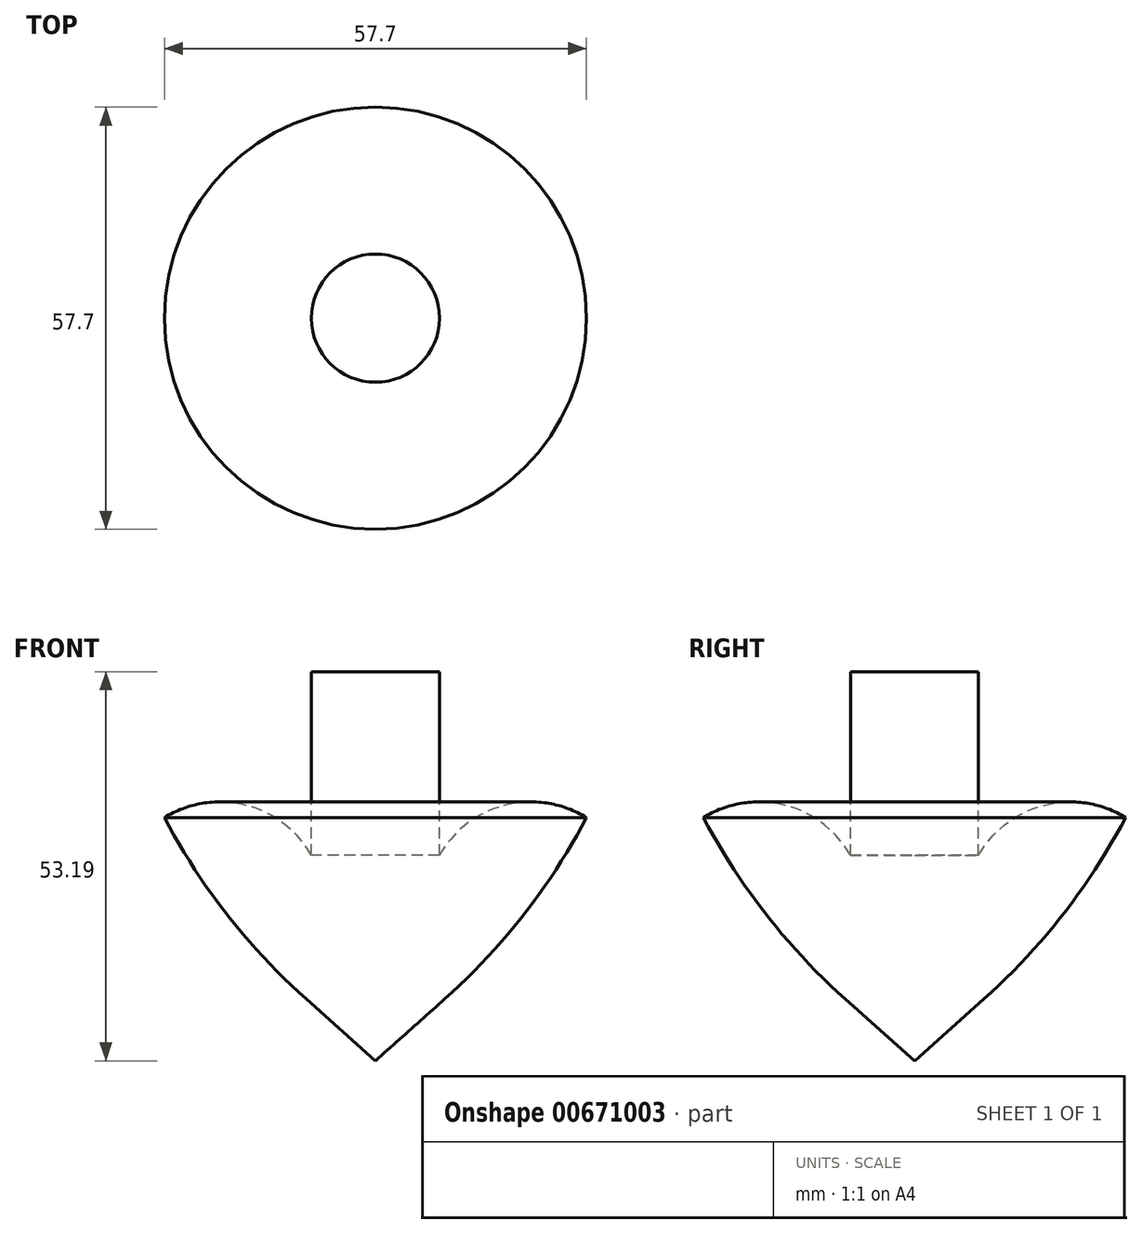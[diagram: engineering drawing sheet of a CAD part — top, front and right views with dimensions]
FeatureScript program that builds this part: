
annotation { "Feature Type Name" : "Feature", "Feature Type Description" : "" }
export const myFeature = defineFeature(function(context is Context, id is Id, definition is map)
    precondition{}
    {
        {
            var Q0;
            Q0=qCreatedBy(makeId("Front.planeOp"),FACE);
            var sketch = newSketch(context, id + "F0", { "sketchPlane" : qUnion([Q0])});
            skLineSegment(sketch, "E0", {"start": v(0, 0) * mm, "end": v(9.48, 8.46) * mm});
            skArc(sketch, "E1", {"start": v(9.48, 8.46) * mm, "mid": v(20.28, 20) * mm, "end": v(28.85, 33.28) * mm});
            skArc(sketch, "E2", {"start": v(28.85, 33.28) * mm, "mid": v(17.71, 34.95) * mm, "end": v(8.76, 28.11) * mm});
            skLineSegment(sketch, "E3", {"start": v(8.76, 28.11) * mm, "end": v(8.76, 53.19) * mm});
            skLineSegment(sketch, "E4", {"start": v(8.76, 53.19) * mm, "end": v(0, 53.19) * mm});
            skLineSegment(sketch, "E5", {"start": v(0, 53.19) * mm, "end": v(0, 0) * mm});
            skSolve(sketch);
        }
        {
            var Q0;
            Q0=makeQuery(id+"F0.imprint","IMPRINT",FACE,{"disambiguationData":[TD([[makeQuery(id+"F0.imprint","IMPRINT",EDGE,{"derivedFrom":sQuery(id+"F0.wireOp",EDGE,"E0")}),1.0]])]});
            var Q1;
            Q1=sQuery(id+"F0.wireOp",EDGE,"E5");
            revolve(context, id + "F1", {"entities" : qUnion([Q0]), "axis" : qUnion([Q1]), "revolveType" : RevolveType.FULL});
        }
    });
